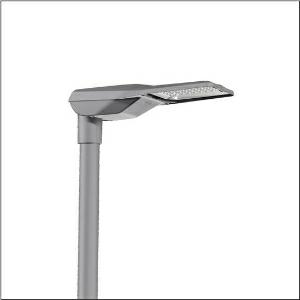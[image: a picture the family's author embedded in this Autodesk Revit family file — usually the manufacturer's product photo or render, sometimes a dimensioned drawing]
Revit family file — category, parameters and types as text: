
# Revit family: streetlight_sl_21_iq_mini___pl52_5xe2h41g08hb_e5d0
name_source: partatom
category: Lighting Fixtures
units: mm (PartAtom-declared; Revit-internal decimal feet)

## family parameters
Cut with Voids When Loaded = No
Host = Face
Light Source = No
Part Type = Normal
Room Calculation Point = No
Round Connector Dimension = Use Diameter
Shared = No

## types (1)
- --- (1 x LED, 9690 lm, 70.9 W, 4000K)
    Apparent Load = 71 VA
    CIE Flux Codes = 27 59 98 100 100
    Color Rendering = 70
    Color Temperature = 4000K
    Default Elevation = 1800 mm
    Description = Streetlight SL 21 iQ mini, mast luminaire, primary light control with lens, of PMMA, primary optical cover: cover, of toughened safety glass, transparent, light distribution: PL52, light emission: direct distribution, primary light characteristic: asymmetric, installation type: post-top, side-entry, LED, High Power LED, rated luminous flux: 9.690lm, luminous efficacy: 137lm/W, light colour: 740, colour temperature: 4000K, control gear: iQ Street-Remote, control: Street-Remote, Auto-Match, Temp-Guard, Lumen-Switch, Night-Set, Smart-Wire, Light-Fading, Desk-Remote (wireless, voltage-free reading and setting of iQ features in the workshop via application-optimized NFC function/RFID function), optimised constant luminous flux control (CLO 2.0), pre-setting: linear dimming characteristic, mains connection: 220..240V, AC, 50/60Hz, start of lifetime: 71W, end of service life: 75W, reduction: 31W, luminaire housing, of diecast aluminium, powder-coated, SITECO metallic grey (DB 702S), corrosivity category C5 high according to DIN EN ISO 12944, please order mast flange separately, inclination adjustable: 0°, 5°, 10°, 15°, sealing non-destructively replaceable, multi-level sealing system, length: 628mm, width: 235mm, height: 110mm, mast flange for spigot size: 42mm (side-entry): 5XC10008XM4, 60/48mm (side-entry/post-top): 5XC10108XM2, 76/60mm (side-entry/post-top): 5XC10108XM1, mounting height: 4..8m, protection rating (complete): IP66, insulation class (complete): insulation class II (safety insulation), certification: CE, ENEC, ENEC+, VDE, impact resistance: IK10, permissible operating ambient temperature for outdoor applications: -40..+50°C, standard-compliant lighting for roads and squares, packaging unit: 1 piece

Light Distribution: PL52
    Height = 110 mm
    Lamp = 1 x LED
    Lamp Light Flux = 9690 lm
    Lamp Power = 70.9 W
    Lamp count = 1
    Length = 625 mm
    Luminous efficacy = 137 lm/W
    Manufacturer = Siteco
    ModVariant = No
    Model = 5XE2H41G08HB
    Number of Poles = 1
    OnlyDefault = Yes
    Power Factor = 1
    Product Name = Streetlight SL 21 iQ mini | PL52
    Product group = mast luminaire | pylon top
    ProductGroupID = 6100
    Protection Class = Protection class II
    Protection Degree = IP 66
    RLX_Detail_Level = 1
    RLX_Emergency_Light_Flux = 0 lm
    RLX_Emergency_Type = 0
    RLX_Emergency_Type_DB = No
    RlxData = <blob elided: 35969 chars, md5=8ecb38ac>
    Socket = socket
    Standby Power = 0 W
    System Light Flux = 9690 lm
    System Power = 71 W
    Type Comments = factory setting: luminous flux: 100 % | dim-lin: 254 | 711 mA
    Type Image = l_1003519.jpg
    URL = http://relux.com
    VarID = @adj_157831
    Voltage = 0 V
    Weight = 0.00 kg
    Width = 234 mm

## geometry (parser evidence)
native form markers: Blend x4, Sweep x9
no freeform markers — native parametric forms only
